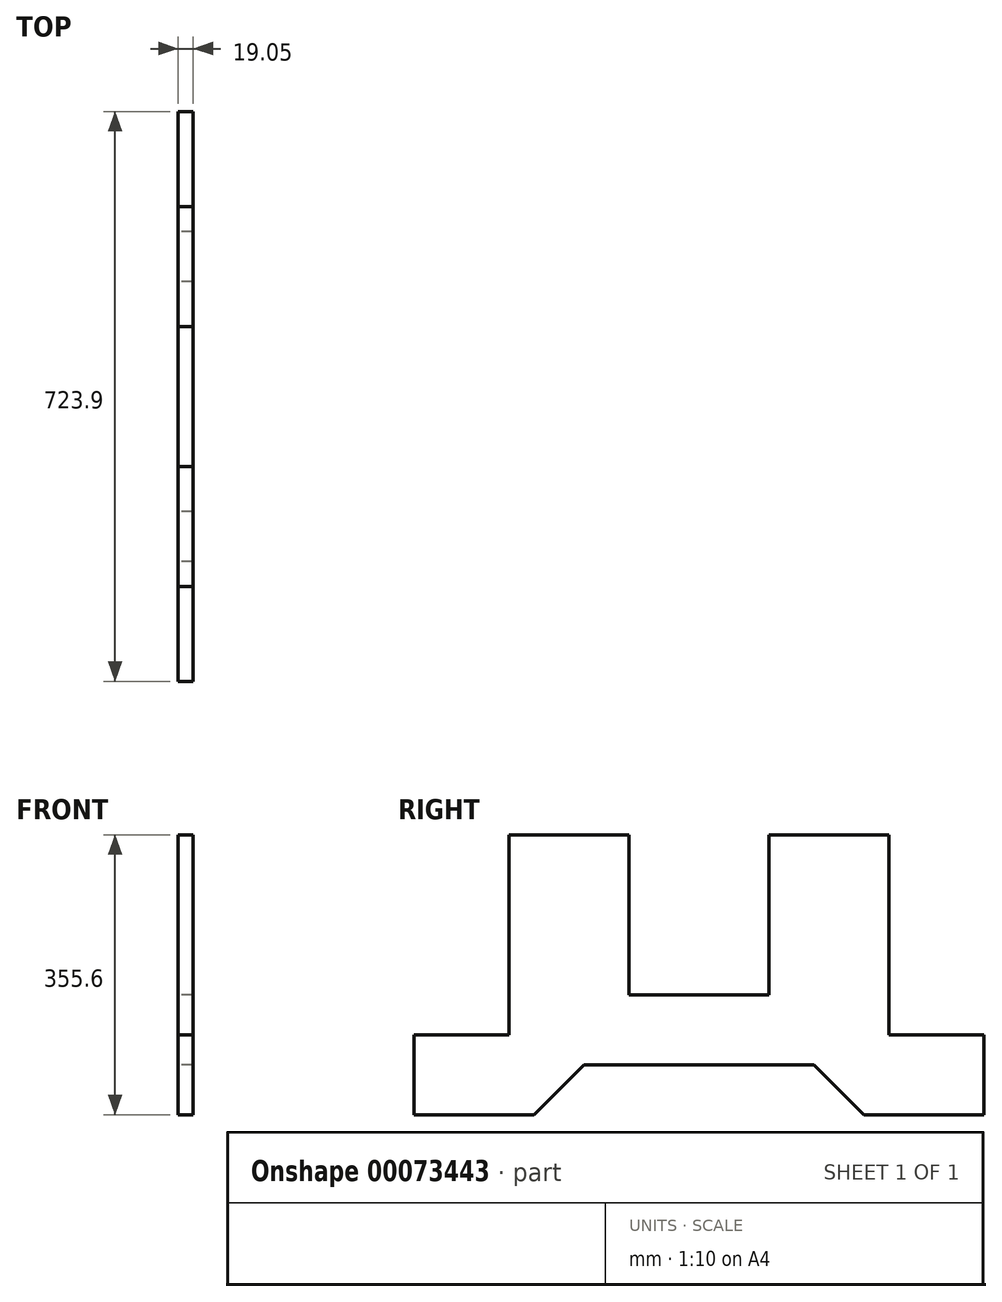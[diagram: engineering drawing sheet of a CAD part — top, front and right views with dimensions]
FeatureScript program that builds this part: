
annotation { "Feature Type Name" : "Feature", "Feature Type Description" : "" }
export const myFeature = defineFeature(function(context is Context, id is Id, definition is map)
    precondition{}
    {
        {
            var Q0;
            Q0=qCreatedBy(makeId("Right.planeOp"),FACE);
            var sketch = newSketch(context, id + "F0", { "sketchPlane" : qUnion([Q0])});
            skLineSegment(sketch, "E0", {"start": v(0, 254) * mm, "end": v(0, 0) * mm});
            skLineSegment(sketch, "E1", {"start": v(0, 0) * mm, "end": v(120.65, 0) * mm});
            skLineSegment(sketch, "E2", {"start": v(120.65, 0) * mm, "end": v(120.65, -101.6) * mm});
            skLineSegment(sketch, "E3", {"start": v(120.65, -101.6) * mm, "end": v(-31.75, -101.6) * mm});
            skLineSegment(sketch, "E4", {"start": v(-31.75, -101.6) * mm, "end": v(-95.25, -38.1) * mm});
            skLineSegment(sketch, "E5", {"start": v(-95.25, -38.1) * mm, "end": v(-387.35, -38.1) * mm});
            skLineSegment(sketch, "E6", {"start": v(-387.35, -38.1) * mm, "end": v(-450.85, -101.6) * mm});
            skLineSegment(sketch, "E7", {"start": v(-450.85, -101.6) * mm, "end": v(-603.25, -101.6) * mm});
            skLineSegment(sketch, "E8", {"start": v(-603.25, -101.6) * mm, "end": v(-603.25, 0) * mm});
            skLineSegment(sketch, "E9", {"start": v(-603.25, 0) * mm, "end": v(-482.6, 0) * mm});
            skLineSegment(sketch, "E10", {"start": v(-482.6, 0) * mm, "end": v(-482.6, 254) * mm});
            skLineSegment(sketch, "E11", {"start": v(-482.6, 254) * mm, "end": v(-330.2, 254) * mm});
            skLineSegment(sketch, "E12", {"start": v(-330.2, 254) * mm, "end": v(-330.2, 50.8) * mm});
            skLineSegment(sketch, "E13", {"start": v(-330.2, 50.8) * mm, "end": v(-152.4, 50.8) * mm});
            skLineSegment(sketch, "E14", {"start": v(-152.4, 50.8) * mm, "end": v(-152.4, 254) * mm});
            skLineSegment(sketch, "E15", {"start": v(-152.4, 254) * mm, "end": v(0, 254) * mm});
            skSolve(sketch);
        }
        {
            var Q0;
            Q0 = qSketchRegion(id + "F0", true);
            extrude(context, id + "F1", {"entities" : qUnion([Q0]), "endBound" : BoundingType.SYMMETRIC, "depth" : 12.7 * mm});
        }
        {
            var Q0;
            Q0 = qSketchRegion(id + "F0", true);
            extrude(context, id + "F2", {"entities" : qUnion([Q0]), "operationType" : NewBodyOperationType.ADD, "depth" : 12.7 * mm});
        }
    });
